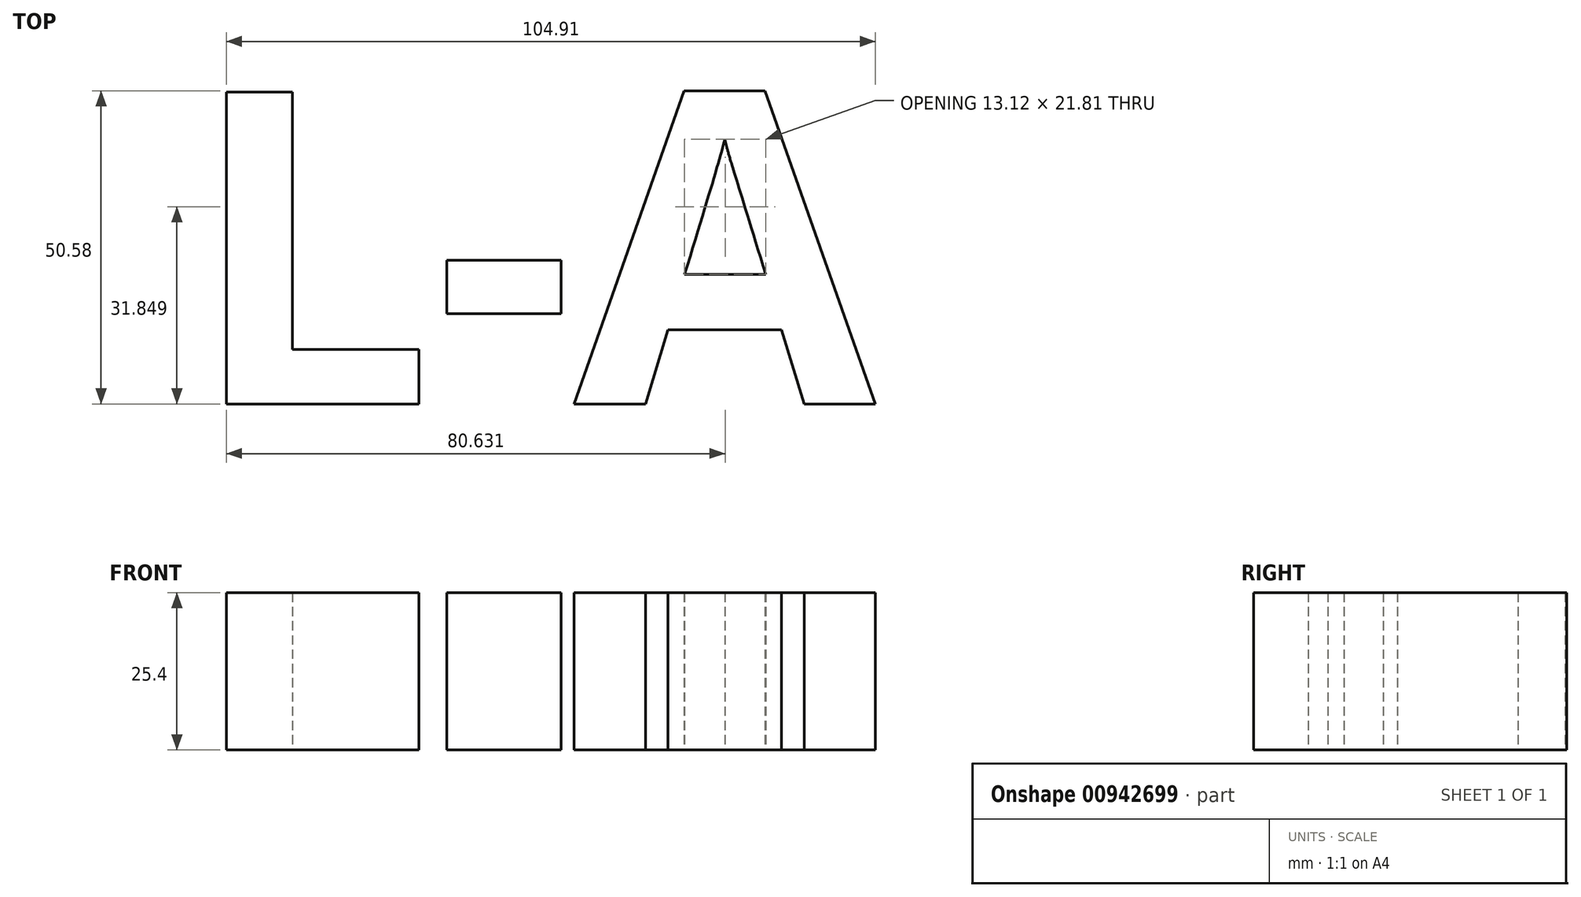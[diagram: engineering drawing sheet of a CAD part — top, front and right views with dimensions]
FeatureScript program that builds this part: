
annotation { "Feature Type Name" : "Feature", "Feature Type Description" : "" }
export const myFeature = defineFeature(function(context is Context, id is Id, definition is map)
    precondition{}
    {
        {
            var Q0;
            Q0=qCreatedBy(makeId("Top.planeOp"),FACE);
            var sketch = newSketch(context, id + "F0", { "sketchPlane" : qUnion([Q0])});
            skText(sketch, "E0", { "text": "L-A", "fontName": "OpenSans-Bold.ttf"});
            const initialGuessF0  = {"E0": [-0.02385, -0.0289, 1, 0, 0.0508]};
            skSetInitialGuess(sketch, initialGuessF0);
            skSolve(sketch);
        }
        {
            var Q0;
            Q0 = qSketchRegion(id + "F0", true);
            extrude(context, id + "F1", {"entities" : qUnion([Q0]), "depth" : 25.4 * mm, "offsetDistance" : 25.4 * mm});
        }
    });
